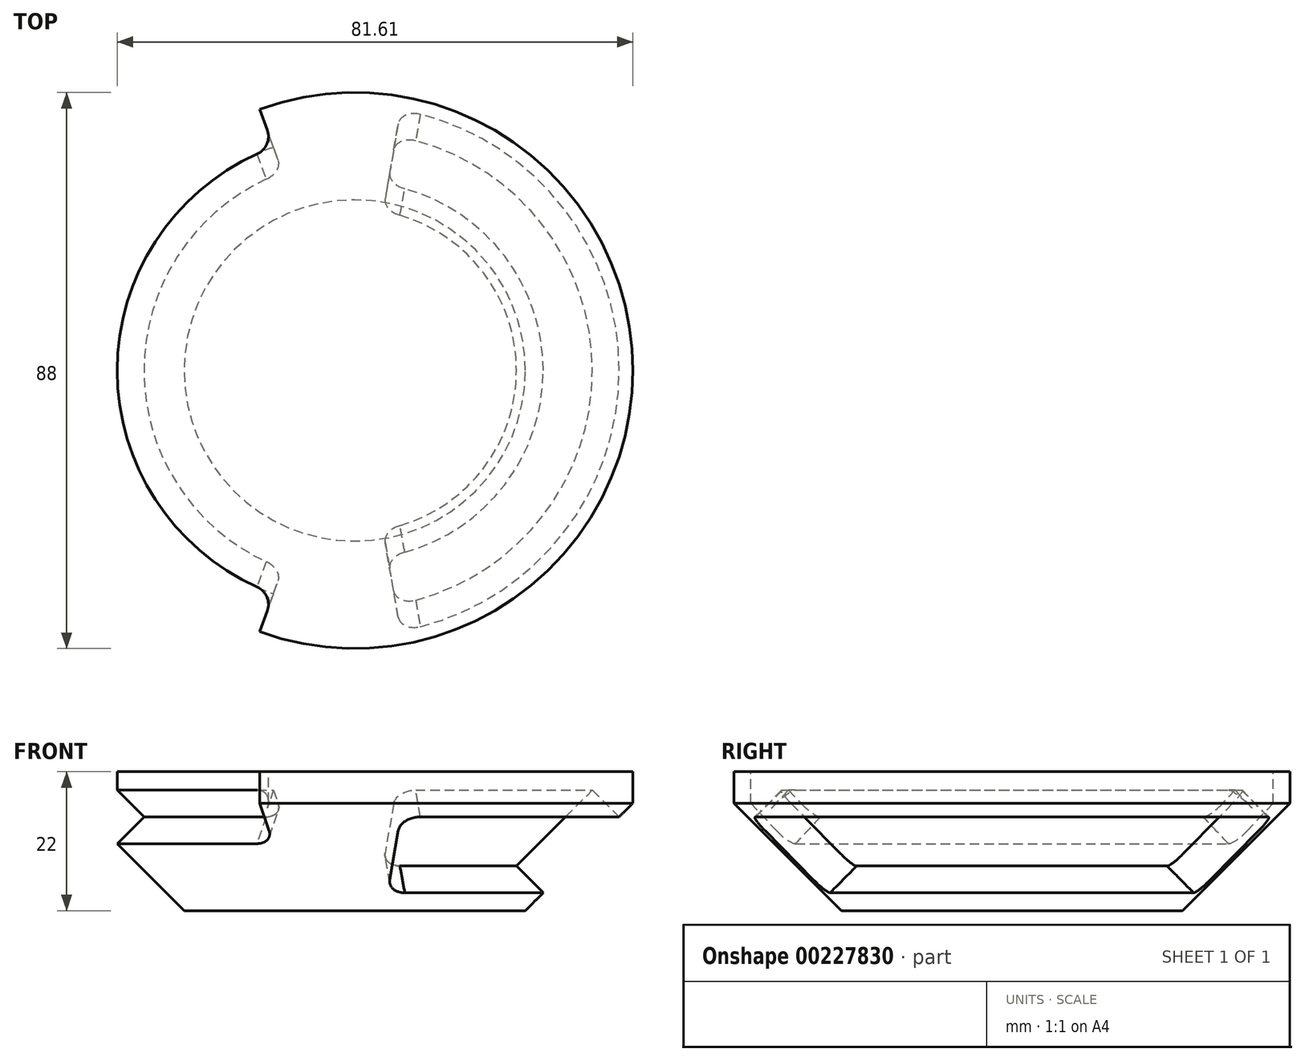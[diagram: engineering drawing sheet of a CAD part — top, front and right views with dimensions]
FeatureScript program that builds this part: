
annotation { "Feature Type Name" : "Feature", "Feature Type Description" : "" }
export const myFeature = defineFeature(function(context is Context, id is Id, definition is map)
    precondition{}
    {
        {
            var Q0;
            Q0=qCreatedBy(makeId("Front.planeOp"),FACE);
            var sketch = newSketch(context, id + "F0", { "sketchPlane" : qUnion([Q0])});
            skLineSegment(sketch, "E0", {"start": v(0, 70.12) * mm, "end": v(0, -51.14) * mm, "construction": true});
            skLineSegment(sketch, "E1", {"start": v(-27, -2) * mm, "end": v(-44, 15) * mm});
            skLineSegment(sketch, "E2", {"start": v(-44, 20) * mm, "end": v(0, 20) * mm});
            skLineSegment(sketch, "E3.trimOffspring", {"start": v(-44, 15) * mm, "end": v(-44, 20) * mm});
            skLineSegment(sketch, "E4", {"start": v(0, 20) * mm, "end": v(0, -2) * mm});
            skLineSegment(sketch, "E5.trimOffspring", {"start": v(-27, -2) * mm, "end": v(0, -2) * mm});
            skSolve(sketch);
        }
        {
            var Q0;
            {var subQ0=sQuery(id+"F0.wireOp",EDGE,"E1");Q0=makeQuery(id+"F0.imprint","IMPRINT",FACE,{"disambiguationData":[TD([[makeQuery(id+"F0.imprint","IMPRINT",EDGE,{"derivedFrom":subQ0}),-1.0]])]});}
            var Q1;
            Q1=sQuery(id+"F0.wireOp",EDGE,"E0");
            revolve(context, id + "F1", {"entities" : qUnion([Q0]), "axis" : qUnion([Q1]), "revolveType" : RevolveType.FULL});
        }
        {
            var Q0;
            Q0=qCreatedBy(makeId("Front.planeOp"),FACE);
            var sketch = newSketch(context, id + "F2", { "sketchPlane" : qUnion([Q0])});
            skLineSegment(sketch, "E6", {"start": v(-33.36, 12.85) * mm, "end": v(-42.7, 3.51) * mm});
            skLineSegment(sketch, "E7", {"start": v(-37.6, 17.1) * mm, "end": v(-46.94, 7.75) * mm});
            skLineSegment(sketch, "E8", {"start": v(-37.6, 17.1) * mm, "end": v(-33.36, 12.85) * mm});
            skLineSegment(sketch, "E9", {"start": v(-46.94, 7.75) * mm, "end": v(-42.7, 3.51) * mm});
            skSolve(sketch);
        }
        {
            var Q0;
            Q0=qCreatedBy(makeId("Front.planeOp"),FACE);
            var sketch = newSketch(context, id + "F3", { "sketchPlane" : qUnion([Q0])});
            skLineSegment(sketch, "E10.0", {"start": v(-37.6, 8.6) * mm, "end": v(-37.6, 25) * mm});
            skLineSegment(sketch, "E11.0", {"start": v(-27, -2) * mm, "end": v(-44, 15) * mm, "construction": true});
            skLineSegment(sketch, "E12", {"start": v(-46, 25) * mm, "end": v(-46, 8.6) * mm});
            skLineSegment(sketch, "E13", {"start": v(-37.6, 8.6) * mm, "end": v(-46, 8.6) * mm});
            skLineSegment(sketch, "E14.0", {"start": v(-44, 20) * mm, "end": v(0, 20) * mm, "construction": true});
            skLineSegment(sketch, "E15", {"start": v(-37.6, 25) * mm, "end": v(-46, 25) * mm});
            skSolve(sketch);
        }
        {
            var Q0;
            Q0 = qSketchRegion(id + "F3", true);
            var Q1;
            Q1=sQuery(id+"F0.wireOp",EDGE,"E0");
            revolve(context, id + "F4", {"entities" : qUnion([Q0]), "axis" : qUnion([Q1]), "revolveType" : RevolveType.TWO_DIRECTIONS, "angle" : 70 * degree, "angleBack" : 290 * degree});
        }
        {
            var Q0;
            Q0=qCreatedBy(makeId("Front.planeOp"),FACE);
            var sketch = newSketch(context, id + "F5", { "sketchPlane" : qUnion([Q0])});
            skLineSegment(sketch, "E16", {"start": v(-25.59, 5.07) * mm, "end": v(-36.9, -6.24) * mm});
            skLineSegment(sketch, "E17", {"start": v(-37.6, 17.1) * mm, "end": v(-48.92, 5.78) * mm});
            skLineSegment(sketch, "E18", {"start": v(-37.6, 17.1) * mm, "end": v(-25.59, 5.07) * mm});
            skLineSegment(sketch, "E19", {"start": v(-48.92, 5.78) * mm, "end": v(-36.9, -6.24) * mm});
            skSolve(sketch);
        }
        {
            var Q0;
            Q0 = qSketchRegion(id + "F5", true);
            var Q1;
            Q1=sQuery(id+"F0.wireOp",EDGE,"E4");
            revolve(context, id + "F6", {"entities" : qUnion([Q0]), "axis" : qUnion([Q1]), "revolveType" : RevolveType.TWO_DIRECTIONS, "angle" : 260 * degree, "angleBack" : 100 * degree});
        }
        {
            var Q0;
            Q0 = qSketchRegion(id + "F2", true);
            var Q1;
            Q1=sQuery(id+"F0.wireOp",EDGE,"E4");
            revolve(context, id + "F7", {"entities" : qUnion([Q0]), "axis" : qUnion([Q1]), "revolveType" : RevolveType.TWO_DIRECTIONS, "angle" : 70 * degree, "angleBack" : 290 * degree});
        }
        {
            var Q0;
            Q0=makeQuery(id+"F7.opRevolve","CAP_EDGE",EDGE,{"disambiguationData":[OSD([sQuery(id+"F2.wireOp",EDGE,"E6")])],"isStart":true});
            var Q1;
            Q1=makeQuery(id+"F7.opRevolve","CAP_EDGE",EDGE,{"disambiguationData":[OSD([sQuery(id+"F2.wireOp",EDGE,"E6")])],"isStart":false});
            var Q2;
            Q2=makeQuery(id+"F4.opRevolve","CAP_EDGE",EDGE,{"disambiguationData":[OSD([sQuery(id+"F3.wireOp",EDGE,"E10.0")])],"isStart":false});
            var Q3;
            Q3=makeQuery(id+"F4.opRevolve","CAP_EDGE",EDGE,{"disambiguationData":[OSD([sQuery(id+"F3.wireOp",EDGE,"E10.0")])],"isStart":true});
            fillet(context, id + "F8", {"entities" : qUnion([Q0, Q1, Q2, Q3]), "radius" : 3 * mm, "tangentPropagation" : true, "allowEdgeOverflow" : false});
        }
        {
            var Q0;
            Q0=makeQuery(id+"F6.opRevolve","CAP_EDGE",EDGE,{"disambiguationData":[OSD([sQuery(id+"F5.wireOp",EDGE,"E16")])],"isStart":true});
            var Q1;
            Q1=makeQuery(id+"F6.opRevolve","CAP_EDGE",EDGE,{"disambiguationData":[OSD([sQuery(id+"F5.wireOp",EDGE,"E17")])],"isStart":true});
            var Q2;
            Q2=makeQuery(id+"F6.opRevolve","CAP_EDGE",EDGE,{"disambiguationData":[OSD([sQuery(id+"F5.wireOp",EDGE,"E17")])],"isStart":false});
            var Q3;
            Q3=makeQuery(id+"F6.opRevolve","CAP_EDGE",EDGE,{"disambiguationData":[OSD([sQuery(id+"F5.wireOp",EDGE,"E16")])],"isStart":false});
            fillet(context, id + "F9", {"entities" : qUnion([Q0, Q1, Q2, Q3]), "radius" : 3 * mm, "tangentPropagation" : true, "allowEdgeOverflow" : false});
        }
        {
            var Q0;
            Q0=makeQuery(id+"F7.opRevolve","SWEPT_BODY",BODY,{"disambiguationData":[OSD([sQuery(id+"F2.wireOp",EDGE,"E6"),sQuery(id+"F2.wireOp",EDGE,"E7"),sQuery(id+"F2.wireOp",EDGE,"E8"),sQuery(id+"F2.wireOp",EDGE,"E9")])]});
            var Q1;
            Q1=makeQuery(id+"F4.opRevolve","SWEPT_BODY",BODY,{"disambiguationData":[OSD([sQuery(id+"F3.wireOp",EDGE,"E10.0"),sQuery(id+"F3.wireOp",EDGE,"E12"),sQuery(id+"F3.wireOp",EDGE,"E13"),sQuery(id+"F3.wireOp",EDGE,"E15")])]});
            var Q2;
            Q2=makeQuery(id+"F6.opRevolve","SWEPT_BODY",BODY,{"disambiguationData":[OSD([sQuery(id+"F5.wireOp",EDGE,"E16"),sQuery(id+"F5.wireOp",EDGE,"E17"),sQuery(id+"F5.wireOp",EDGE,"E18"),sQuery(id+"F5.wireOp",EDGE,"E19")])]});
            var Q3;
            Q3=makeQuery(id+"F1.opRevolve","SWEPT_BODY",BODY,{"disambiguationData":[OSD([sQuery(id+"F0.wireOp",EDGE,"E1"),sQuery(id+"F0.wireOp",EDGE,"E2"),sQuery(id+"F0.wireOp",EDGE,"E3.trimOffspring"),sQuery(id+"F0.wireOp",EDGE,"E4"),sQuery(id+"F0.wireOp",EDGE,"E5.trimOffspring")])]});
            booleanBodies(context, id + "F10", {"operationType" : BooleanOperationType.SUBTRACTION, "tools" : qUnion([Q0, Q1, Q2]), "targets" : qUnion([Q3])});
        }
    });
